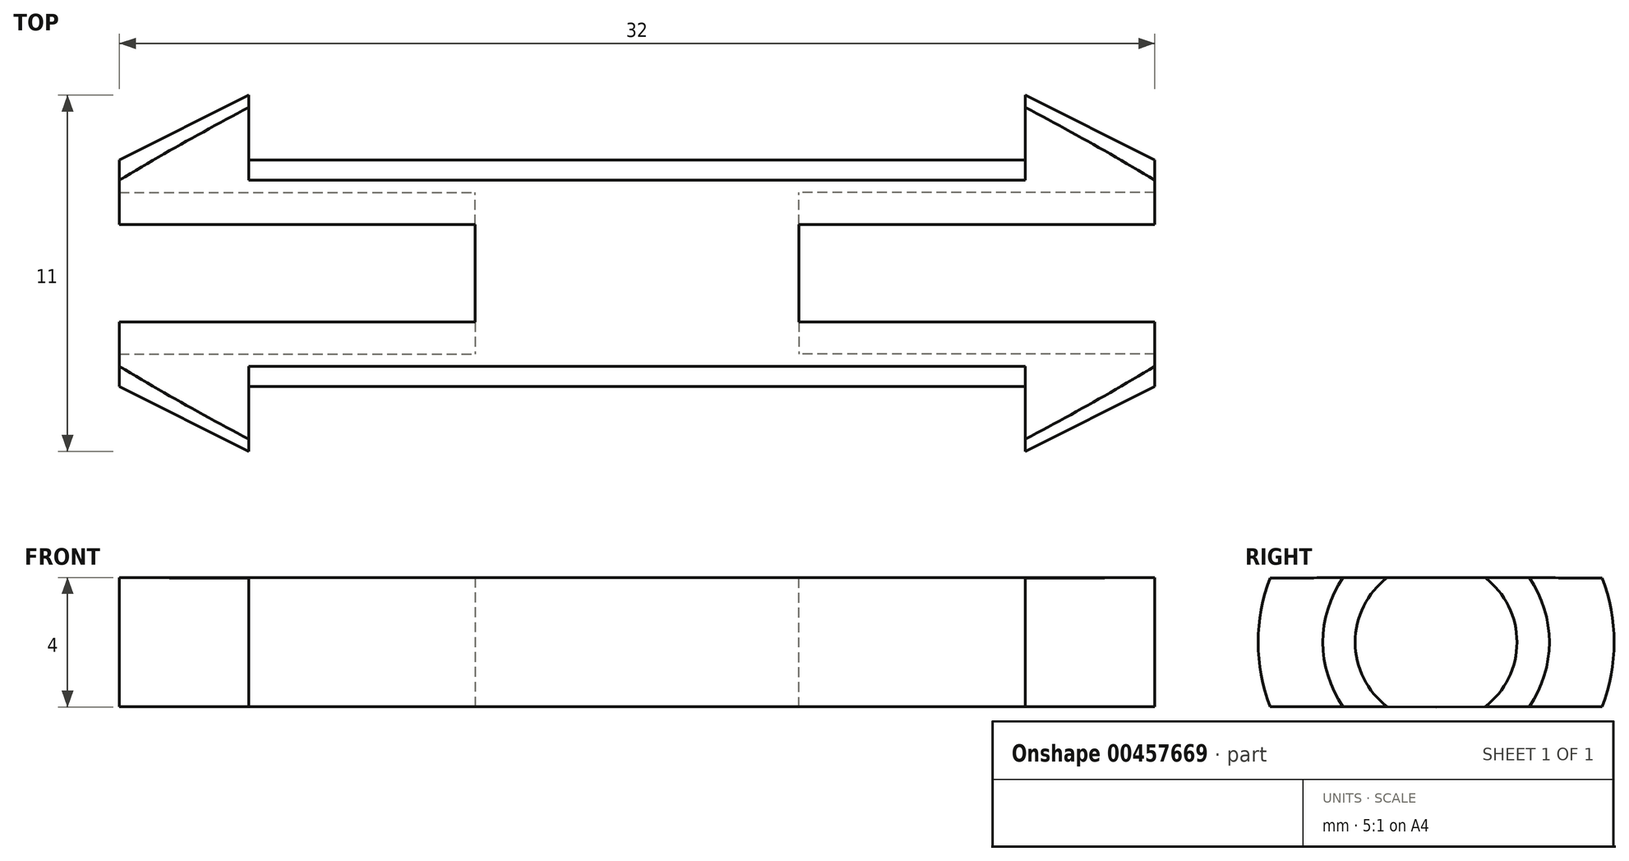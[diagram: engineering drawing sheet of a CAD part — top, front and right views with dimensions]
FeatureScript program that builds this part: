
annotation { "Feature Type Name" : "Feature", "Feature Type Description" : "" }
export const myFeature = defineFeature(function(context is Context, id is Id, definition is map)
    precondition{}
    {
        {
            var Q0;
            Q0=qCreatedBy(makeId("Top.planeOp"),FACE);
            var sketch = newSketch(context, id + "F0", { "sketchPlane" : qUnion([Q0])});
            skLineSegment(sketch, "E0.bottom", {"start": v(0, 3.5) * mm, "end": v(5, 3.5) * mm});
            skLineSegment(sketch, "E0.top", {"start": v(0, 0) * mm, "end": v(5, 0) * mm});
            skLineSegment(sketch, "E0.left", {"start": v(0, 3.5) * mm, "end": v(0, 0) * mm});
            skLineSegment(sketch, "E0.right", {"start": v(5, 3.5) * mm, "end": v(5, 0) * mm});
            skLineSegment(sketch, "E1.bottom", {"start": v(5, 3.5) * mm, "end": v(16, 3.5) * mm});
            skLineSegment(sketch, "E1.top", {"start": v(5, 2.5) * mm, "end": v(16, 2.5) * mm});
            skLineSegment(sketch, "E1.left", {"start": v(5, 3.5) * mm, "end": v(5, 2.5) * mm});
            skLineSegment(sketch, "E1.right", {"start": v(16, 3.5) * mm, "end": v(16, 2.5) * mm});
            skLineSegment(sketch, "E2", {"start": v(16, 3.5) * mm, "end": v(12, 5.5) * mm});
            skLineSegment(sketch, "E3", {"start": v(12, 5.5) * mm, "end": v(12, 3.5) * mm});
            skSolve(sketch);
        }
        {
            var Q0;
            Q0 = qSketchRegion(id + "F0", true);
            var Q1;
            Q1=sQuery(id+"F0.wireOp",EDGE,"E0.top");
            revolve(context, id + "F1", {"entities" : qUnion([Q0]), "axis" : qUnion([Q1]), "revolveType" : RevolveType.FULL});
        }
        {
            var Q0;
            Q0=qCreatedBy(makeId("Front.planeOp"),FACE);
            var sketch = newSketch(context, id + "F2", { "sketchPlane" : qUnion([Q0])});
            skLineSegment(sketch, "E4.bottom", {"start": v(0, 17) * mm, "end": v(21, 17) * mm});
            skLineSegment(sketch, "E4.top", {"start": v(0, 2) * mm, "end": v(21, 2) * mm});
            skLineSegment(sketch, "E4.left", {"start": v(0, 17) * mm, "end": v(0, 2) * mm});
            skLineSegment(sketch, "E4.right", {"start": v(21, 17) * mm, "end": v(21, 2) * mm});
            skLineSegment(sketch, "E5.bottom", {"start": v(0, -17) * mm, "end": v(21, -17) * mm});
            skLineSegment(sketch, "E5.top", {"start": v(0, -2) * mm, "end": v(21, -2) * mm});
            skLineSegment(sketch, "E5.left", {"start": v(0, -17) * mm, "end": v(0, -2) * mm});
            skLineSegment(sketch, "E5.right", {"start": v(21, -17) * mm, "end": v(21, -2) * mm});
            skSolve(sketch);
        }
        {
            var Q0;
            Q0 = qSketchRegion(id + "F2", true);
            extrude(context, id + "F3", {"entities" : qUnion([Q0]), "operationType" : NewBodyOperationType.REMOVE, "endBound" : BoundingType.SYMMETRIC, "oppositeDirection" : true, "depth" : 21 * mm, "hasDraft" : true, "draftAngle" : 0.16 * degree});
        }
        {
            var Q0;
            Q0=makeQuery(id+"F1.opRevolve","SWEPT_BODY",BODY,{"disambiguationData":[OSD([sQuery(id+"F0.wireOp",EDGE,"E0.bottom"),sQuery(id+"F0.wireOp",EDGE,"E0.top"),sQuery(id+"F0.wireOp",EDGE,"E0.left"),sQuery(id+"F0.wireOp",EDGE,"E0.right"),sQuery(id+"F0.wireOp",EDGE,"E1.bottom"),sQuery(id+"F0.wireOp",EDGE,"E1.top"),sQuery(id+"F0.wireOp",EDGE,"E1.right"),sQuery(id+"F0.wireOp",EDGE,"E2"),sQuery(id+"F0.wireOp",EDGE,"E3")])]});
            var Q1;
            Q1=qCreatedBy(makeId("Right.planeOp"),FACE);
            mirror(context, id + "F4", {"operationType" : NewBodyOperationType.ADD, "entities" : qUnion([Q0]), "mirrorPlane" : qUnion([Q1])});
        }
    });
